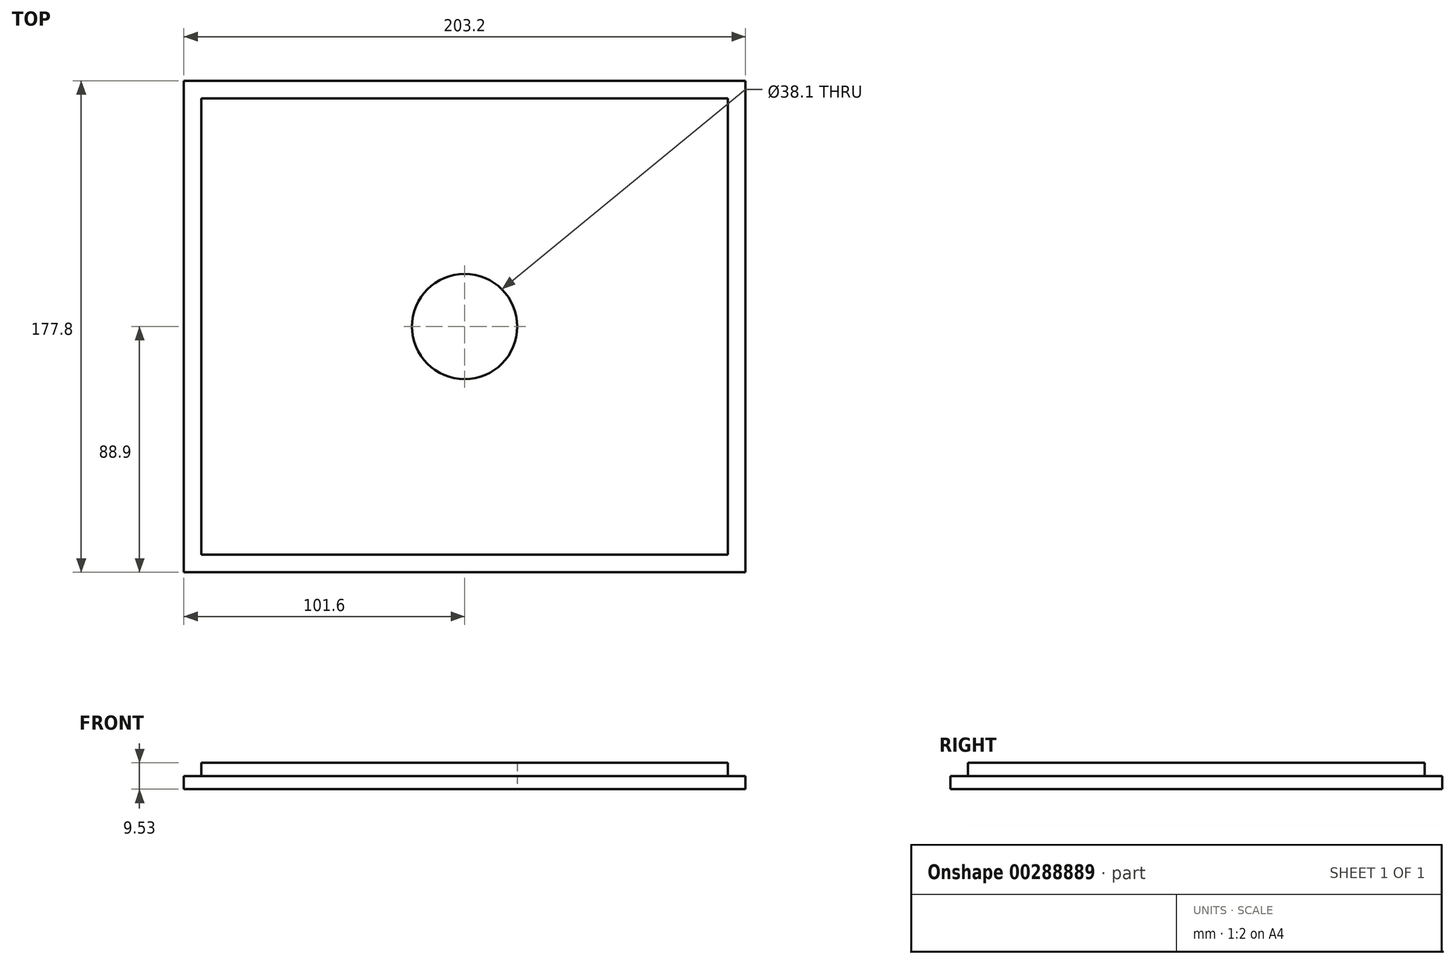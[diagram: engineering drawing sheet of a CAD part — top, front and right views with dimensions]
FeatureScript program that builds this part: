
annotation { "Feature Type Name" : "Feature", "Feature Type Description" : "" }
export const myFeature = defineFeature(function(context is Context, id is Id, definition is map)
    precondition{}
    {
        {
            var Q0;
            Q0=qCreatedBy(makeId("Top.planeOp"),FACE);
            var sketch = newSketch(context, id + "F0", { "sketchPlane" : qUnion([Q0])});
            skLineSegment(sketch, "E0.bottom", {"start": v(101.6, 88.9) * mm, "end": v(-101.6, 88.9) * mm});
            skLineSegment(sketch, "E0.top", {"start": v(101.6, -88.9) * mm, "end": v(-101.6, -88.9) * mm});
            skLineSegment(sketch, "E0.left", {"start": v(101.6, 88.9) * mm, "end": v(101.6, -88.9) * mm});
            skLineSegment(sketch, "E0.right", {"start": v(-101.6, 88.9) * mm, "end": v(-101.6, -88.9) * mm});
            skPoint(sketch, "E0.middle", {"position": v(0, 0) * mm});
            skLineSegment(sketch, "E1.bottom", {"start": v(95.25, 82.55) * mm, "end": v(-95.25, 82.55) * mm});
            skLineSegment(sketch, "E1.top", {"start": v(95.25, -82.55) * mm, "end": v(-95.25, -82.55) * mm});
            skLineSegment(sketch, "E1.left", {"start": v(95.25, 82.55) * mm, "end": v(95.25, -82.55) * mm});
            skLineSegment(sketch, "E1.right", {"start": v(-95.25, 82.55) * mm, "end": v(-95.25, -82.55) * mm});
            skCircle(sketch, "E2", {"center": v(0, 0) * mm, "radius": 19.05 * mm});
            skSolve(sketch);
        }
        {
            var Q0;
            Q0=makeQuery(id+"F0.imprint","IMPRINT",FACE,{"disambiguationData":[TD([[makeQuery(id+"F0.imprint","IMPRINT",EDGE,{"derivedFrom":sQuery(id+"F0.wireOp",EDGE,"E1.bottom")}),1.0]])]});
            extrude(context, id + "F1", {"entities" : qUnion([Q0]), "depth" : 9.52 * mm});
        }
        {
            var Q0;
            Q0=makeQuery(id+"F0.imprint","IMPRINT",FACE,{"disambiguationData":[TD([[makeQuery(id+"F0.imprint","IMPRINT",EDGE,{"derivedFrom":sQuery(id+"F0.wireOp",EDGE,"E0.bottom")}),1.0]])]});
            extrude(context, id + "F2", {"entities" : qUnion([Q0]), "operationType" : NewBodyOperationType.ADD, "depth" : 4.76 * mm});
        }
    });
